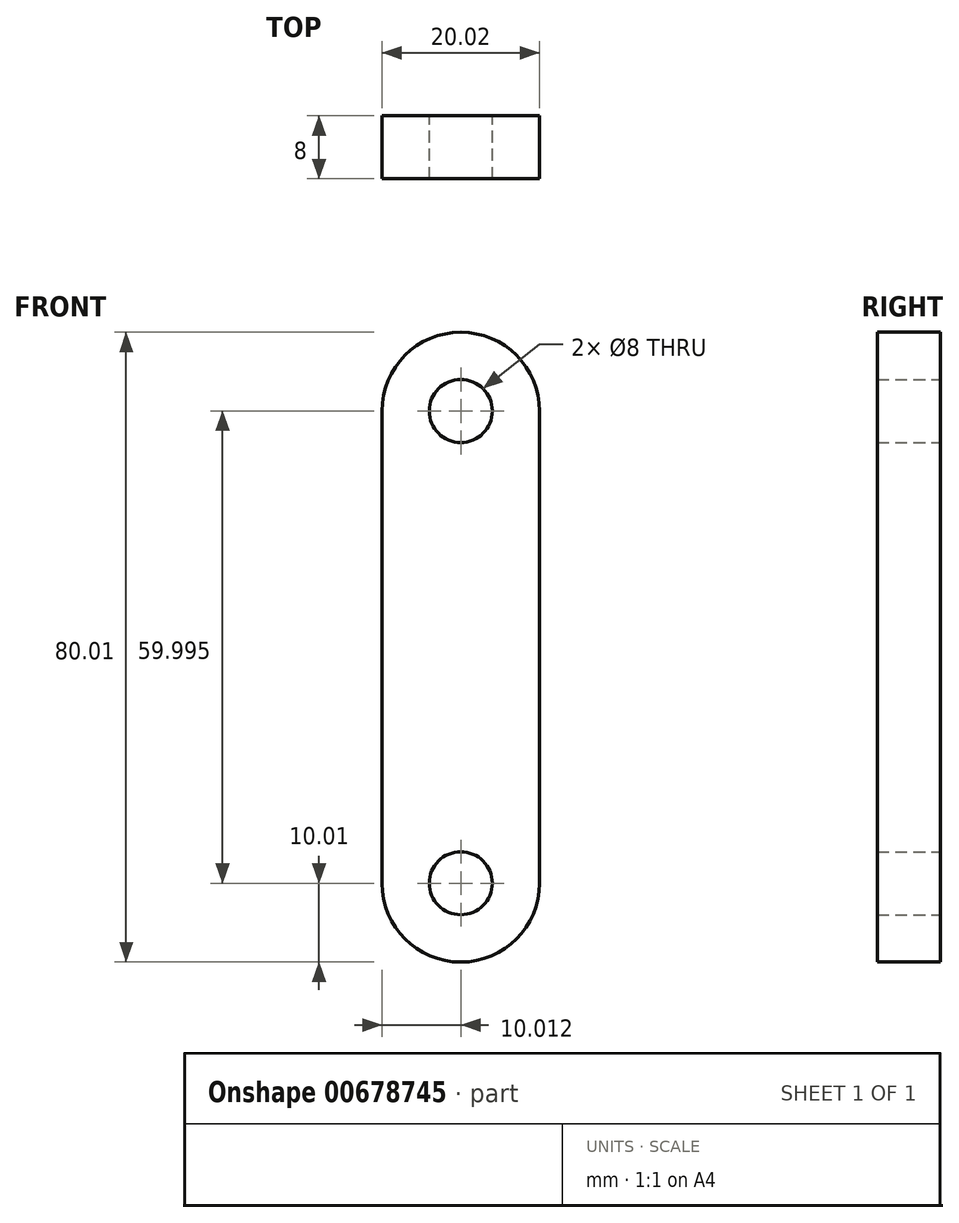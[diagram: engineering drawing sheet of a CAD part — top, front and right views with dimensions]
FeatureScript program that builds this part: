
annotation { "Feature Type Name" : "Feature", "Feature Type Description" : "" }
export const myFeature = defineFeature(function(context is Context, id is Id, definition is map)
    precondition{}
    {
        {
            var Q0;
            Q0=qCreatedBy(makeId("Front.planeOp"),FACE);
            var sketch = newSketch(context, id + "F0", { "sketchPlane" : qUnion([Q0])});
            skLineSegment(sketch, "E0.bottom", {"start": v(0, 0) * mm, "end": v(-20.02, 0) * mm});
            skLineSegment(sketch, "E0.top", {"start": v(0, 60) * mm, "end": v(-20.02, 60) * mm});
            skLineSegment(sketch, "E0.left", {"start": v(0, 0) * mm, "end": v(0, 60) * mm});
            skLineSegment(sketch, "E0.right", {"start": v(-20.02, 0) * mm, "end": v(-20.02, 60) * mm});
            skCircle(sketch, "E1", {"center": v(-10, 60) * mm, "radius": 10 * mm});
            skCircle(sketch, "E2", {"center": v(-10, 0) * mm, "radius": 10 * mm});
            skCircle(sketch, "E3", {"center": v(-10, 0) * mm, "radius": 4 * mm});
            skCircle(sketch, "E4", {"center": v(-10, 60) * mm, "radius": 4 * mm});
            skSolve(sketch);
        }
        {
            var Q0;
            {var subQ1=sQuery(id+"F0.wireOp",EDGE,"E0.top");var subQ3=sQuery(id+"F0.wireOp",EDGE,"E4");var subQ4=makeQuery(id+"F0.imprint","INTERSECT",VERTEX,{"disambiguationData":[OD(0.0)],"derivedFrom":[subQ1,subQ3]});Q0=makeQuery(id+"F0.imprint","IMPRINT",FACE,{"disambiguationData":[TD([[makeQuery(id+"F0.imprint","IMPRINT",EDGE,{"disambiguationData":[TD([[subQ4,-1.0]])],"derivedFrom":subQ3}),-1.0]])]});}
            var Q1;
            {var subQ1=sQuery(id+"F0.wireOp",EDGE,"E0.top");var subQ3=sQuery(id+"F0.wireOp",EDGE,"E4");var subQ4=makeQuery(id+"F0.imprint","INTERSECT",VERTEX,{"disambiguationData":[OD(0.0)],"derivedFrom":[subQ1,subQ3]});Q1=makeQuery(id+"F0.imprint","IMPRINT",FACE,{"disambiguationData":[TD([[makeQuery(id+"F0.imprint","IMPRINT",EDGE,{"disambiguationData":[TD([[subQ4,1.0]])],"derivedFrom":subQ3}),-1.0]])]});}
            var Q2;
            {var subQ0=sQuery(id+"F0.wireOp",EDGE,"E0.left");Q2=makeQuery(id+"F0.imprint","IMPRINT",FACE,{"disambiguationData":[TD([[makeQuery(id+"F0.imprint","IMPRINT",EDGE,{"derivedFrom":subQ0}),1.0]])]});}
            var Q3;
            {var subQ1=sQuery(id+"F0.wireOp",EDGE,"E0.bottom");var subQ3=sQuery(id+"F0.wireOp",EDGE,"E3");var subQ4=makeQuery(id+"F0.imprint","INTERSECT",VERTEX,{"disambiguationData":[OD(0.0)],"derivedFrom":[subQ1,subQ3]});Q3=makeQuery(id+"F0.imprint","IMPRINT",FACE,{"disambiguationData":[TD([[makeQuery(id+"F0.imprint","IMPRINT",EDGE,{"disambiguationData":[TD([[subQ4,-1.0]])],"derivedFrom":subQ3}),-1.0]])]});}
            var Q4;
            {var subQ1=sQuery(id+"F0.wireOp",EDGE,"E0.bottom");var subQ3=sQuery(id+"F0.wireOp",EDGE,"E3");var subQ4=makeQuery(id+"F0.imprint","INTERSECT",VERTEX,{"disambiguationData":[OD(0.0)],"derivedFrom":[subQ1,subQ3]});Q4=makeQuery(id+"F0.imprint","IMPRINT",FACE,{"disambiguationData":[TD([[makeQuery(id+"F0.imprint","IMPRINT",EDGE,{"disambiguationData":[TD([[subQ4,1.0]])],"derivedFrom":subQ3}),-1.0]])]});}
            extrude(context, id + "F1", {"entities" : qUnion([Q0, Q1, Q2, Q3, Q4]), "depth" : 8 * mm, "offsetDistance" : 25 * mm});
        }
    });
